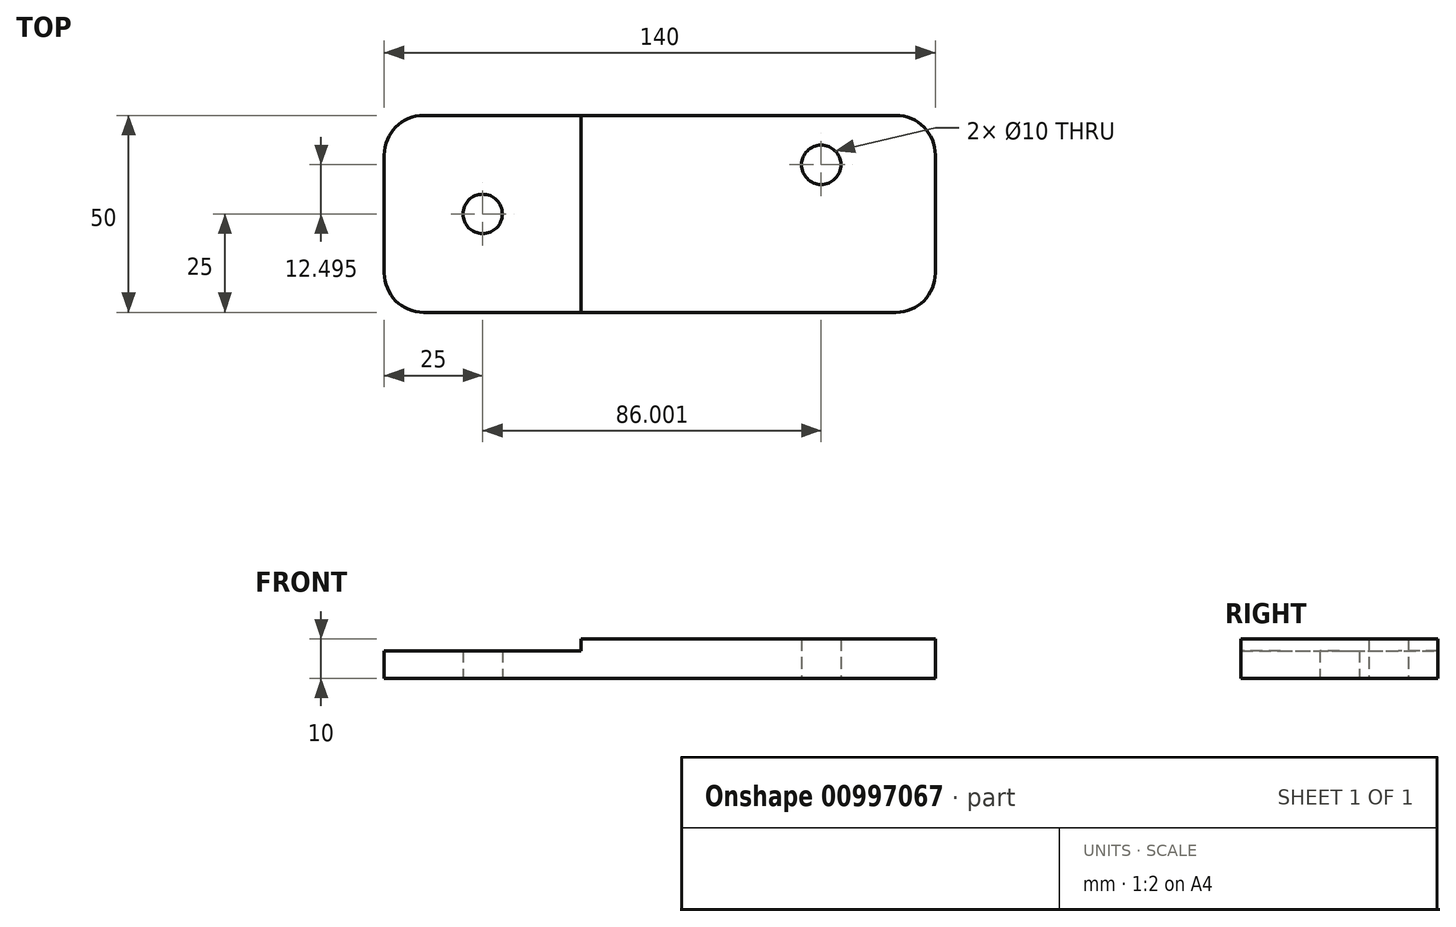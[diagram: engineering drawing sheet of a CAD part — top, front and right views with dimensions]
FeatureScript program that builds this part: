
annotation { "Feature Type Name" : "Feature", "Feature Type Description" : "" }
export const myFeature = defineFeature(function(context is Context, id is Id, definition is map)
    precondition{}
    {
        {
            var Q0;
            Q0=qCreatedBy(makeId("Front.planeOp"),FACE);
            var sketch = newSketch(context, id + "F0", { "sketchPlane" : qUnion([Q0])});
            skLineSegment(sketch, "E0", {"start": v(0, 0) * mm, "end": v(0, -7) * mm});
            skLineSegment(sketch, "E1", {"start": v(0, -7) * mm, "end": v(140, -7) * mm});
            skLineSegment(sketch, "E2", {"start": v(140, -7) * mm, "end": v(140, 3) * mm});
            skLineSegment(sketch, "E3", {"start": v(0, 0) * mm, "end": v(50, 0) * mm});
            skLineSegment(sketch, "E4", {"start": v(50, 0) * mm, "end": v(50, 3) * mm});
            skLineSegment(sketch, "E5", {"start": v(50, 3) * mm, "end": v(140, 3) * mm});
            skSolve(sketch);
        }
        {
            var Q0;
            Q0=makeQuery(id+"F0.imprint","IMPRINT",FACE,{"disambiguationData":[TD([[makeQuery(id+"F0.imprint","IMPRINT",EDGE,{"derivedFrom":sQuery(id+"F0.wireOp",EDGE,"E0")}),1.0]])]});
            extrude(context, id + "F1", {"entities" : qUnion([Q0]), "depth" : 50 * mm, "offsetDistance" : 25 * mm});
        }
        {
            var Q0;
            Q0=makeQuery(id+"F1.opExtrude","CAP_EDGE",EDGE,{"disambiguationData":[OSD([sQuery(id+"F0.wireOp",EDGE,"E0")])],"isStart":false});
            var Q1;
            Q1=makeQuery(id+"F1.opExtrude","CAP_EDGE",EDGE,{"disambiguationData":[OSD([sQuery(id+"F0.wireOp",EDGE,"E0")])],"isStart":true});
            var Q2;
            Q2=makeQuery(id+"F1.opExtrude","CAP_EDGE",EDGE,{"disambiguationData":[OSD([sQuery(id+"F0.wireOp",EDGE,"E2")])],"isStart":true});
            var Q3;
            Q3=makeQuery(id+"F1.opExtrude","CAP_EDGE",EDGE,{"disambiguationData":[OSD([sQuery(id+"F0.wireOp",EDGE,"E2")])],"isStart":false});
            fillet(context, id + "F2", {"entities" : qUnion([Q0, Q1, Q2, Q3]), "radius" : 10 * mm, "tangentPropagation" : true, "allowEdgeOverflow" : false});
        }
        {
            var Q0;
            Q0=makeQuery(id+"F1.opExtrude","SWEPT_FACE",FACE,{"disambiguationData":[OSD([sQuery(id+"F0.wireOp",EDGE,"E1")])]});
            var sketch = newSketch(context, id + "F3", { "sketchPlane" : qUnion([Q0])});
            skCircle(sketch, "E6", {"center": v(25, 25) * mm, "radius": 5 * mm});
            skEllipse(sketch, "E7.0", {"center": v(111, 12.5) * mm, "majorRadius": 5 * mm, "minorRadius": 5 * mm, "majorAxis": v(-1, 0.12), "construction": true});
            skCircle(sketch, "E8", {"center": v(111, 12.5) * mm, "radius": 5 * mm});
            skSolve(sketch);
        }
        {
            var Q0;
            Q0=makeQuery(id+"F3.imprint","IMPRINT",FACE,{"disambiguationData":[TD([[makeQuery(id+"F3.imprint","IMPRINT",EDGE,{"derivedFrom":sQuery(id+"F3.wireOp",EDGE,"E6")}),1.0]])]});
            var Q1;
            Q1=makeQuery(id+"F3.imprint","IMPRINT",FACE,{"disambiguationData":[TD([[makeQuery(id+"F3.imprint","IMPRINT",EDGE,{"derivedFrom":sQuery(id+"F3.wireOp",EDGE,"E7.0")}),1.0]])]});
            var Q2;
            Q2=makeQuery(id+"F1.opExtrude","SWEPT_FACE",FACE,{"disambiguationData":[OSD([sQuery(id+"F0.wireOp",EDGE,"E3")])]});
            extrude(context, id + "F4", {"entities" : qUnion([Q0, Q1]), "operationType" : NewBodyOperationType.REMOVE, "oppositeDirection" : true, "depth" : 25 * mm, "endBoundEntityFace" : qUnion([Q2]), "offsetDistance" : 25 * mm});
        }
        {
            var Q0;
            Q0=sQuery(id+"F3.wireOp",VERTEX,"E7.0.center");
            var Q1;
            Q1=makeQuery(id+"F1.opExtrude","SWEPT_BODY",BODY,{"disambiguationData":[OSD([sQuery(id+"F0.wireOp",EDGE,"E0"),sQuery(id+"F0.wireOp",EDGE,"E1"),sQuery(id+"F0.wireOp",EDGE,"E2"),sQuery(id+"F0.wireOp",EDGE,"E3"),sQuery(id+"F0.wireOp",EDGE,"E4"),sQuery(id+"F0.wireOp",EDGE,"E5")])]});
            hole(context, id + "F5", {"style" : HoleStyle.SIMPLE, "endStyle" : HoleEndStyle.THROUGH, "holeDiameter" : 10 * mm, "majorDiameter" : 5 * mm, "tappedDepth" : 12 * mm, "tapClearance" : 3, "locations" : qUnion([Q0]), "scope" : qUnion([Q1])});
        }
    });
